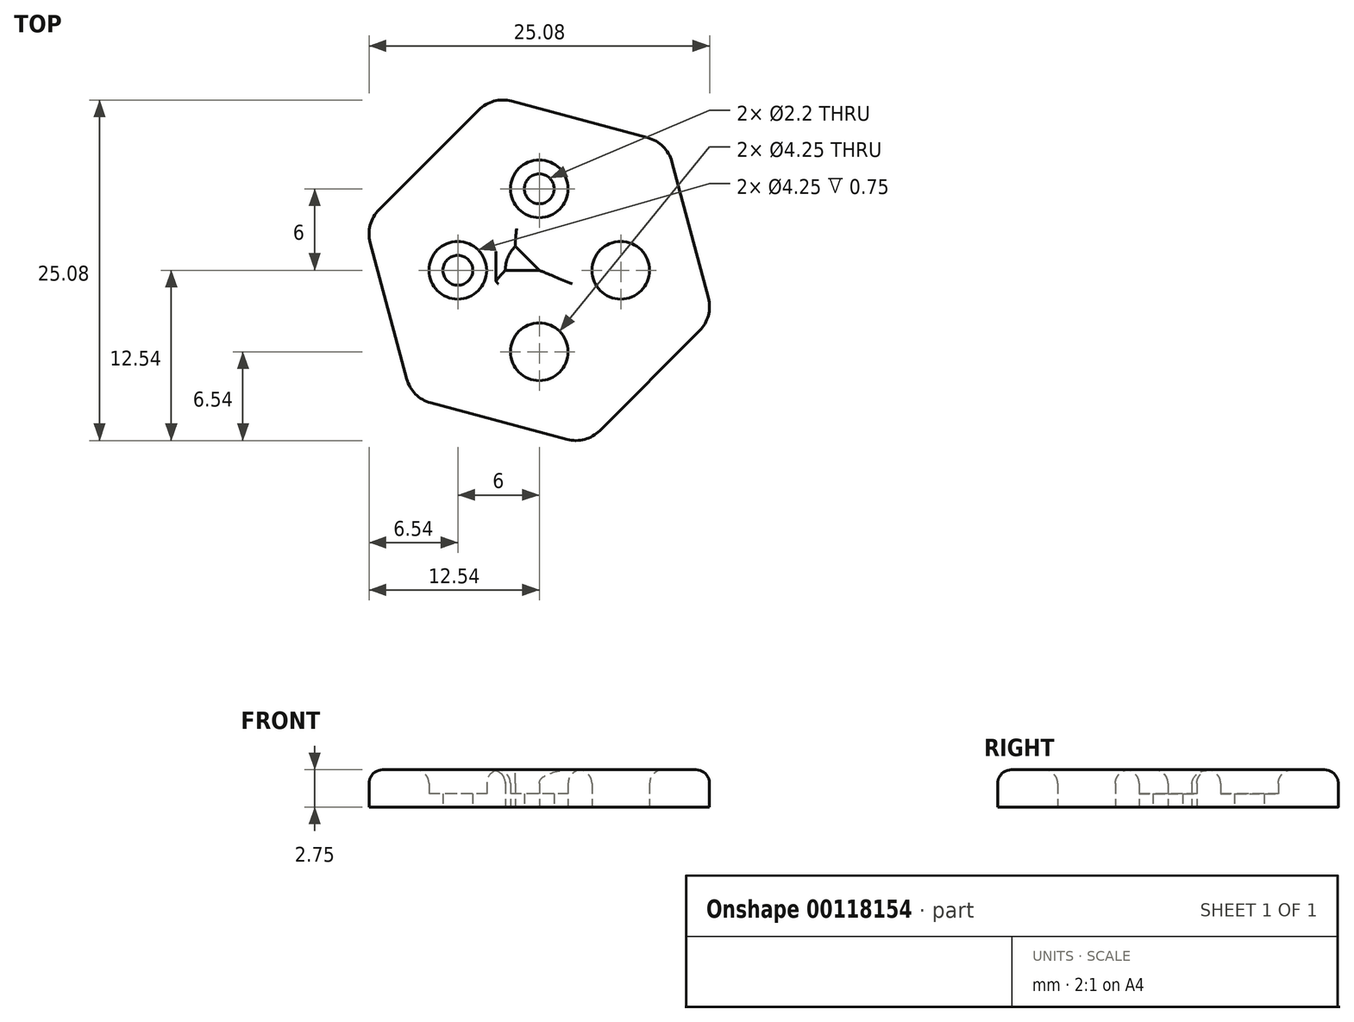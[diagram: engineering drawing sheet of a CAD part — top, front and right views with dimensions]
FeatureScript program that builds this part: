
annotation { "Feature Type Name" : "Feature", "Feature Type Description" : "" }
export const myFeature = defineFeature(function(context is Context, id is Id, definition is map)
    precondition{}
    {
        {
            var Q0;
            Q0=qCreatedBy(makeId("Top.planeOp"),FACE);
            var sketch = newSketch(context, id + "F0", { "sketchPlane" : qUnion([Q0])});
            skCircle(sketch, "E0", {"center": v(0, 0) * mm, "radius": 11.5 * mm});
            skLineSegment(sketch, "E1", {"start": v(0, 11.5) * mm, "end": v(0, -11.5) * mm});
            skLineSegment(sketch, "E2", {"start": v(-19.9, 0) * mm, "end": v(23, 0) * mm});
            skCircle(sketch, "E3", {"center": v(-6, 0) * mm, "radius": 1.1 * mm});
            skCircle(sketch, "E4", {"center": v(0, 6) * mm, "radius": 1.1 * mm});
            skCircle(sketch, "E5", {"center": v(6, 0) * mm, "radius": 1.1 * mm});
            skCircle(sketch, "E6", {"center": v(0, -6) * mm, "radius": 1.1 * mm});
            skCircle(sketch, "E7", {"center": v(-6, 0) * mm, "radius": 2.12 * mm});
            skCircle(sketch, "E8", {"center": v(0, -6) * mm, "radius": 2.12 * mm});
            skCircle(sketch, "E9", {"center": v(6, 0) * mm, "radius": 2.12 * mm});
            skCircle(sketch, "E10", {"center": v(0, 6) * mm, "radius": 2.12 * mm});
            skCircle(sketch, "E11.cCircle", {"center": v(0, 0) * mm, "radius": 11.5 * mm, "construction": true});
            skLineSegment(sketch, "E11.0", {"start": v(-12.83, 3.44) * mm, "end": v(-3.44, 12.83) * mm});
            skLineSegment(sketch, "E11.1", {"start": v(-3.44, 12.83) * mm, "end": v(9.39, 9.39) * mm});
            skLineSegment(sketch, "E11.2", {"start": v(9.39, 9.39) * mm, "end": v(12.83, -3.44) * mm});
            skLineSegment(sketch, "E11.3", {"start": v(12.83, -3.44) * mm, "end": v(3.44, -12.83) * mm});
            skLineSegment(sketch, "E11.4", {"start": v(3.44, -12.83) * mm, "end": v(-9.39, -9.39) * mm});
            skLineSegment(sketch, "E11.5", {"start": v(-9.39, -9.39) * mm, "end": v(-12.83, 3.44) * mm});
            skPoint(sketch, "E11.0.midPoint", {"position": v(-8.13, 8.13) * mm});
            skCircle(sketch, "E12", {"center": v(0, 0) * mm, "radius": 2.5 * mm});
            skLineSegment(sketch, "E13", {"start": v(-11.14, 11.14) * mm, "end": v(0, 0) * mm});
            skSolve(sketch);
        }
        {
            var Q0;
            Q0 = qSketchRegion(id + "F0", true);
            var Q1;
            {var subQ0=sQuery(id+"F0.wireOp",EDGE,"E7");var subQ1=sQuery(id+"F0.wireOp",EDGE,"E2");var subQ2=makeQuery(id+"F0.imprint","INTERSECT",VERTEX,{"disambiguationData":[OD(0.0)],"derivedFrom":[subQ1,subQ0]});Q1=makeQuery(id+"F0.imprint","IMPRINT",FACE,{"disambiguationData":[TD([[makeQuery(id+"F0.imprint","IMPRINT",EDGE,{"disambiguationData":[TD([[subQ2,-1.0]])],"derivedFrom":subQ1}),1.0]])]});}
            var Q2;
            {var subQ0=sQuery(id+"F0.wireOp",EDGE,"E7");var subQ1=sQuery(id+"F0.wireOp",EDGE,"E2");var subQ2=makeQuery(id+"F0.imprint","INTERSECT",VERTEX,{"disambiguationData":[OD(0.0)],"derivedFrom":[subQ1,subQ0]});Q2=makeQuery(id+"F0.imprint","IMPRINT",FACE,{"disambiguationData":[TD([[makeQuery(id+"F0.imprint","IMPRINT",EDGE,{"disambiguationData":[TD([[subQ2,-1.0]])],"derivedFrom":subQ1}),-1.0]])]});}
            var Q3;
            {var subQ0=sQuery(id+"F0.wireOp",EDGE,"E10");var subQ1=sQuery(id+"F0.wireOp",EDGE,"E1");var subQ2=makeQuery(id+"F0.imprint","INTERSECT",VERTEX,{"disambiguationData":[OD(0.0)],"derivedFrom":[subQ1,subQ0]});Q3=makeQuery(id+"F0.imprint","IMPRINT",FACE,{"disambiguationData":[TD([[makeQuery(id+"F0.imprint","IMPRINT",EDGE,{"disambiguationData":[TD([[subQ2,-1.0]])],"derivedFrom":subQ1}),-1.0]])]});}
            var Q4;
            {var subQ0=sQuery(id+"F0.wireOp",EDGE,"E10");var subQ1=sQuery(id+"F0.wireOp",EDGE,"E1");var subQ2=makeQuery(id+"F0.imprint","INTERSECT",VERTEX,{"disambiguationData":[OD(0.0)],"derivedFrom":[subQ1,subQ0]});Q4=makeQuery(id+"F0.imprint","IMPRINT",FACE,{"disambiguationData":[TD([[makeQuery(id+"F0.imprint","IMPRINT",EDGE,{"disambiguationData":[TD([[subQ2,-1.0]])],"derivedFrom":subQ1}),1.0]])]});}
            var Q5;
            {var subQ0=sQuery(id+"F0.wireOp",EDGE,"E9");var subQ1=sQuery(id+"F0.wireOp",EDGE,"E2");var subQ2=makeQuery(id+"F0.imprint","INTERSECT",VERTEX,{"disambiguationData":[OD(0.0)],"derivedFrom":[subQ1,subQ0]});Q5=makeQuery(id+"F0.imprint","IMPRINT",FACE,{"disambiguationData":[TD([[makeQuery(id+"F0.imprint","IMPRINT",EDGE,{"disambiguationData":[TD([[subQ2,-1.0]])],"derivedFrom":subQ1}),1.0]])]});}
            var Q6;
            {var subQ0=sQuery(id+"F0.wireOp",EDGE,"E9");var subQ1=sQuery(id+"F0.wireOp",EDGE,"E2");var subQ2=makeQuery(id+"F0.imprint","INTERSECT",VERTEX,{"disambiguationData":[OD(0.0)],"derivedFrom":[subQ1,subQ0]});Q6=makeQuery(id+"F0.imprint","IMPRINT",FACE,{"disambiguationData":[TD([[makeQuery(id+"F0.imprint","IMPRINT",EDGE,{"disambiguationData":[TD([[subQ2,-1.0]])],"derivedFrom":subQ1}),-1.0]])]});}
            var Q7;
            {var subQ0=sQuery(id+"F0.wireOp",EDGE,"E8");var subQ1=sQuery(id+"F0.wireOp",EDGE,"E1");var subQ2=makeQuery(id+"F0.imprint","INTERSECT",VERTEX,{"disambiguationData":[OD(0.0)],"derivedFrom":[subQ1,subQ0]});Q7=makeQuery(id+"F0.imprint","IMPRINT",FACE,{"disambiguationData":[TD([[makeQuery(id+"F0.imprint","IMPRINT",EDGE,{"disambiguationData":[TD([[subQ2,-1.0]])],"derivedFrom":subQ1}),1.0]])]});}
            var Q8;
            {var subQ0=sQuery(id+"F0.wireOp",EDGE,"E8");var subQ1=sQuery(id+"F0.wireOp",EDGE,"E1");var subQ2=makeQuery(id+"F0.imprint","INTERSECT",VERTEX,{"disambiguationData":[OD(0.0)],"derivedFrom":[subQ1,subQ0]});Q8=makeQuery(id+"F0.imprint","IMPRINT",FACE,{"disambiguationData":[TD([[makeQuery(id+"F0.imprint","IMPRINT",EDGE,{"disambiguationData":[TD([[subQ2,-1.0]])],"derivedFrom":subQ1}),-1.0]])]});}
            var Q9;
            {var subQ1=sQuery(id+"F0.wireOp",EDGE,"E1");var subQ3=sQuery(id+"F0.wireOp",EDGE,"E12");var subQ4=makeQuery(id+"F0.imprint","INTERSECT",VERTEX,{"disambiguationData":[OD(1.0)],"derivedFrom":[subQ1,subQ3]});Q9=makeQuery(id+"F0.imprint","IMPRINT",FACE,{"disambiguationData":[TD([[makeQuery(id+"F0.imprint","IMPRINT",EDGE,{"disambiguationData":[TD([[subQ4,1.0]])],"derivedFrom":subQ3}),1.0]])]});}
            var Q10;
            {var subQ1=sQuery(id+"F0.wireOp",EDGE,"E2");var subQ3=sQuery(id+"F0.wireOp",EDGE,"E12");var subQ4=makeQuery(id+"F0.imprint","INTERSECT",VERTEX,{"disambiguationData":[OD(0.0)],"derivedFrom":[subQ1,subQ3]});Q10=makeQuery(id+"F0.imprint","IMPRINT",FACE,{"disambiguationData":[TD([[makeQuery(id+"F0.imprint","IMPRINT",EDGE,{"disambiguationData":[TD([[subQ4,1.0]])],"derivedFrom":subQ3}),1.0]])]});}
            var Q11;
            {var subQ1=sQuery(id+"F0.wireOp",EDGE,"E1");var subQ3=sQuery(id+"F0.wireOp",EDGE,"E12");var subQ4=makeQuery(id+"F0.imprint","INTERSECT",VERTEX,{"disambiguationData":[OD(0.0)],"derivedFrom":[subQ1,subQ3]});Q11=makeQuery(id+"F0.imprint","IMPRINT",FACE,{"disambiguationData":[TD([[makeQuery(id+"F0.imprint","IMPRINT",EDGE,{"disambiguationData":[TD([[subQ4,-1.0]])],"derivedFrom":subQ3}),1.0]])]});}
            var Q12;
            {var subQ1=sQuery(id+"F0.wireOp",EDGE,"E1");var subQ3=sQuery(id+"F0.wireOp",EDGE,"E12");var subQ4=makeQuery(id+"F0.imprint","INTERSECT",VERTEX,{"disambiguationData":[OD(0.0)],"derivedFrom":[subQ1,subQ3]});Q12=makeQuery(id+"F0.imprint","IMPRINT",FACE,{"disambiguationData":[TD([[makeQuery(id+"F0.imprint","IMPRINT",EDGE,{"disambiguationData":[TD([[subQ4,1.0]])],"derivedFrom":subQ3}),1.0]])]});}
            var Q13;
            {var subQ1=sQuery(id+"F0.wireOp",EDGE,"E1");var subQ3=sQuery(id+"F0.wireOp",EDGE,"E12");var subQ4=makeQuery(id+"F0.imprint","INTERSECT",VERTEX,{"disambiguationData":[OD(1.0)],"derivedFrom":[subQ1,subQ3]});Q13=makeQuery(id+"F0.imprint","IMPRINT",FACE,{"disambiguationData":[TD([[makeQuery(id+"F0.imprint","IMPRINT",EDGE,{"disambiguationData":[TD([[subQ4,-1.0]])],"derivedFrom":subQ3}),1.0]])]});}
            extrude(context, id + "F1", {"entities" : qUnion([Q0, Q1, Q2, Q3, Q4, Q5, Q6, Q7, Q8, Q9, Q10, Q11, Q12, Q13]), "depth" : 1 * mm});
        }
        {
            var Q0;
            Q0 = qSketchRegion(id + "F0", true);
            var Q1;
            {var subQ1=sQuery(id+"F0.wireOp",EDGE,"E1");var subQ3=sQuery(id+"F0.wireOp",EDGE,"E12");var subQ4=makeQuery(id+"F0.imprint","INTERSECT",VERTEX,{"disambiguationData":[OD(0.0)],"derivedFrom":[subQ1,subQ3]});Q1=makeQuery(id+"F0.imprint","IMPRINT",FACE,{"disambiguationData":[TD([[makeQuery(id+"F0.imprint","IMPRINT",EDGE,{"disambiguationData":[TD([[subQ4,-1.0]])],"derivedFrom":subQ3}),1.0]])]});}
            var Q2;
            {var subQ1=sQuery(id+"F0.wireOp",EDGE,"E2");var subQ3=sQuery(id+"F0.wireOp",EDGE,"E12");var subQ4=makeQuery(id+"F0.imprint","INTERSECT",VERTEX,{"disambiguationData":[OD(0.0)],"derivedFrom":[subQ1,subQ3]});Q2=makeQuery(id+"F0.imprint","IMPRINT",FACE,{"disambiguationData":[TD([[makeQuery(id+"F0.imprint","IMPRINT",EDGE,{"disambiguationData":[TD([[subQ4,1.0]])],"derivedFrom":subQ3}),1.0]])]});}
            var Q3;
            {var subQ1=sQuery(id+"F0.wireOp",EDGE,"E1");var subQ3=sQuery(id+"F0.wireOp",EDGE,"E12");var subQ4=makeQuery(id+"F0.imprint","INTERSECT",VERTEX,{"disambiguationData":[OD(1.0)],"derivedFrom":[subQ1,subQ3]});Q3=makeQuery(id+"F0.imprint","IMPRINT",FACE,{"disambiguationData":[TD([[makeQuery(id+"F0.imprint","IMPRINT",EDGE,{"disambiguationData":[TD([[subQ4,1.0]])],"derivedFrom":subQ3}),1.0]])]});}
            var Q4;
            {var subQ1=sQuery(id+"F0.wireOp",EDGE,"E1");var subQ3=sQuery(id+"F0.wireOp",EDGE,"E12");var subQ4=makeQuery(id+"F0.imprint","INTERSECT",VERTEX,{"disambiguationData":[OD(1.0)],"derivedFrom":[subQ1,subQ3]});Q4=makeQuery(id+"F0.imprint","IMPRINT",FACE,{"disambiguationData":[TD([[makeQuery(id+"F0.imprint","IMPRINT",EDGE,{"disambiguationData":[TD([[subQ4,-1.0]])],"derivedFrom":subQ3}),1.0]])]});}
            var Q5;
            {var subQ1=sQuery(id+"F0.wireOp",EDGE,"E1");var subQ3=sQuery(id+"F0.wireOp",EDGE,"E12");var subQ4=makeQuery(id+"F0.imprint","INTERSECT",VERTEX,{"disambiguationData":[OD(0.0)],"derivedFrom":[subQ1,subQ3]});Q5=makeQuery(id+"F0.imprint","IMPRINT",FACE,{"disambiguationData":[TD([[makeQuery(id+"F0.imprint","IMPRINT",EDGE,{"disambiguationData":[TD([[subQ4,1.0]])],"derivedFrom":subQ3}),1.0]])]});}
            extrude(context, id + "F2", {"entities" : qUnion([Q0, Q1, Q2, Q3, Q4, Q5]), "operationType" : NewBodyOperationType.ADD, "depth" : 2.75 * mm});
        }
        {
            var Q0;
            {var subQ0=sQuery(id+"F0.wireOp",EDGE,"E11.1");var subQ1=sQuery(id+"F0.wireOp",EDGE,"E11.0");Q0=makeQuery(id+"F2.boolean.opBoolean","MERGE",EDGE,{"derivedFrom":[makeQuery(id+"F1.opExtrude","SWEPT_EDGE",EDGE,{"disambiguationData":[OSD([subQ1,subQ0])]}),makeQuery(id+"F2.opExtrude","SWEPT_EDGE",EDGE,{"disambiguationData":[OSD([subQ1,subQ0])]})]});}
            var Q1;
            {var subQ0=sQuery(id+"F0.wireOp",EDGE,"E11.5");var subQ1=sQuery(id+"F0.wireOp",EDGE,"E11.0");Q1=makeQuery(id+"F2.boolean.opBoolean","MERGE",EDGE,{"derivedFrom":[makeQuery(id+"F1.opExtrude","SWEPT_EDGE",EDGE,{"disambiguationData":[OSD([subQ1,subQ0])]}),makeQuery(id+"F2.opExtrude","SWEPT_EDGE",EDGE,{"disambiguationData":[OSD([subQ1,subQ0])]})]});}
            var Q2;
            {var subQ0=sQuery(id+"F0.wireOp",EDGE,"E11.5");var subQ1=sQuery(id+"F0.wireOp",EDGE,"E11.4");Q2=makeQuery(id+"F2.boolean.opBoolean","MERGE",EDGE,{"derivedFrom":[makeQuery(id+"F1.opExtrude","SWEPT_EDGE",EDGE,{"disambiguationData":[OSD([subQ1,subQ0])]}),makeQuery(id+"F2.opExtrude","SWEPT_EDGE",EDGE,{"disambiguationData":[OSD([subQ1,subQ0])]})]});}
            var Q3;
            {var subQ0=sQuery(id+"F0.wireOp",EDGE,"E11.4");var subQ1=sQuery(id+"F0.wireOp",EDGE,"E11.3");Q3=makeQuery(id+"F2.boolean.opBoolean","MERGE",EDGE,{"derivedFrom":[makeQuery(id+"F1.opExtrude","SWEPT_EDGE",EDGE,{"disambiguationData":[OSD([subQ1,subQ0])]}),makeQuery(id+"F2.opExtrude","SWEPT_EDGE",EDGE,{"disambiguationData":[OSD([subQ1,subQ0])]})]});}
            var Q4;
            {var subQ0=sQuery(id+"F0.wireOp",EDGE,"E11.3");var subQ1=sQuery(id+"F0.wireOp",EDGE,"E11.2");Q4=makeQuery(id+"F2.boolean.opBoolean","MERGE",EDGE,{"derivedFrom":[makeQuery(id+"F1.opExtrude","SWEPT_EDGE",EDGE,{"disambiguationData":[OSD([subQ1,subQ0])]}),makeQuery(id+"F2.opExtrude","SWEPT_EDGE",EDGE,{"disambiguationData":[OSD([subQ1,subQ0])]})]});}
            var Q5;
            {var subQ0=sQuery(id+"F0.wireOp",EDGE,"E11.2");var subQ1=sQuery(id+"F0.wireOp",EDGE,"E11.1");Q5=makeQuery(id+"F2.boolean.opBoolean","MERGE",EDGE,{"derivedFrom":[makeQuery(id+"F1.opExtrude","SWEPT_EDGE",EDGE,{"disambiguationData":[OSD([subQ1,subQ0])]}),makeQuery(id+"F2.opExtrude","SWEPT_EDGE",EDGE,{"disambiguationData":[OSD([subQ1,subQ0])]})]});}
            fillet(context, id + "F3", {"entities" : qUnion([Q0, Q1, Q2, Q3, Q4, Q5]), "radius" : 2.5 * mm, "tangentPropagation" : true, "allowEdgeOverflow" : false});
        }
        {
            var Q0;
            Q0=makeQuery(id+"F2.opExtrude","CAP_FACE",FACE,{"disambiguationData":[OSD([sQuery(id+"F0.wireOp",EDGE,"E7"),sQuery(id+"F0.wireOp",EDGE,"E8"),sQuery(id+"F0.wireOp",EDGE,"E9"),sQuery(id+"F0.wireOp",EDGE,"E10"),sQuery(id+"F0.wireOp",EDGE,"E11.0"),sQuery(id+"F0.wireOp",EDGE,"E11.1"),sQuery(id+"F0.wireOp",EDGE,"E11.2"),sQuery(id+"F0.wireOp",EDGE,"E11.3"),sQuery(id+"F0.wireOp",EDGE,"E11.4"),sQuery(id+"F0.wireOp",EDGE,"E11.5"),sQuery(id+"F0.wireOp",EDGE,"E12")])],"isStart":false});
            fillet(context, id + "F4", {"entities" : qUnion([Q0]), "radius" : 1 * mm, "tangentPropagation" : true, "allowEdgeOverflow" : false});
        }
    });
